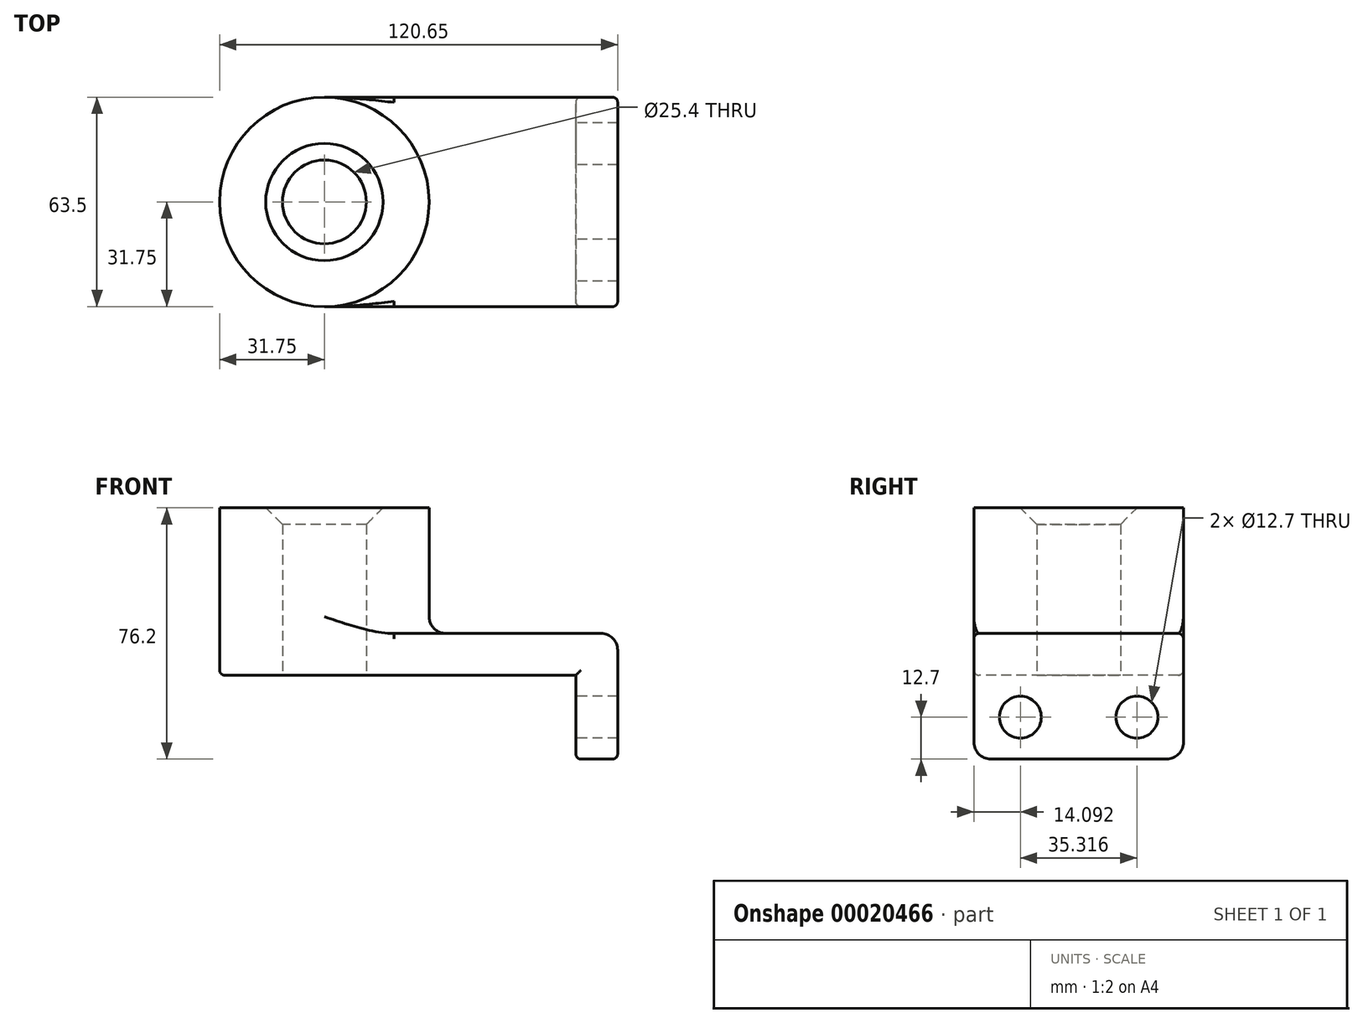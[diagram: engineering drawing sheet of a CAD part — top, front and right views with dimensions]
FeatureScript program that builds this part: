
annotation { "Feature Type Name" : "Feature", "Feature Type Description" : "" }
export const myFeature = defineFeature(function(context is Context, id is Id, definition is map)
    precondition{}
    {
        {
            var Q0;
            Q0=qCreatedBy(makeId("Top.planeOp"),FACE);
            var sketch = newSketch(context, id + "F0", { "sketchPlane" : qUnion([Q0])});
            skLineSegment(sketch, "E0.rect.bottom", {"start": v(-38.1, 31.75) * mm, "end": v(38.1, 31.75) * mm});
            skLineSegment(sketch, "E0.rect.top", {"start": v(-38.1, -31.75) * mm, "end": v(38.1, -31.75) * mm});
            skLineSegment(sketch, "E0.rect.left", {"start": v(-38.1, 31.75) * mm, "end": v(-38.1, -31.75) * mm});
            skLineSegment(sketch, "E0.rect.right", {"start": v(38.1, 31.75) * mm, "end": v(38.1, -31.75) * mm});
            skPoint(sketch, "E0.rect.middle", {"position": v(0, 0) * mm});
            skCircle(sketch, "E1", {"center": v(-38.1, 0) * mm, "radius": 31.75 * mm});
            skCircle(sketch, "E2", {"center": v(-38.1, 0) * mm, "radius": 12.7 * mm});
            skSolve(sketch);
        }
        {
            var Q0;
            {var subQ3=sQuery(id+"F0.wireOp",EDGE,"E0.rect.bottom");Q0=makeQuery(id+"F0.imprint","IMPRINT",FACE,{"disambiguationData":[TD([[makeQuery(id+"F0.imprint","IMPRINT",EDGE,{"derivedFrom":subQ3}),-1.0]])]});}
            var Q1;
            {var subQ0=sQuery(id+"F0.wireOp",EDGE,"E2");var subQ1=sQuery(id+"F0.wireOp",EDGE,"E0.rect.left");var subQ3=makeQuery(id+"F0.imprint","INTERSECT",VERTEX,{"disambiguationData":[OD(0.0)],"derivedFrom":[subQ1,subQ0]});Q1=makeQuery(id+"F0.imprint","IMPRINT",FACE,{"disambiguationData":[TD([[makeQuery(id+"F0.imprint","IMPRINT",EDGE,{"disambiguationData":[TD([[subQ3,-1.0]])],"derivedFrom":subQ0}),-1.0]])]});}
            var Q2;
            {var subQ0=sQuery(id+"F0.wireOp",EDGE,"E2");var subQ1=sQuery(id+"F0.wireOp",EDGE,"E0.rect.left");var subQ3=makeQuery(id+"F0.imprint","INTERSECT",VERTEX,{"disambiguationData":[OD(0.0)],"derivedFrom":[subQ1,subQ0]});Q2=makeQuery(id+"F0.imprint","IMPRINT",FACE,{"disambiguationData":[TD([[makeQuery(id+"F0.imprint","IMPRINT",EDGE,{"disambiguationData":[TD([[subQ3,1.0]])],"derivedFrom":subQ0}),-1.0]])]});}
            extrude(context, id + "F1", {"entities" : qUnion([Q0, Q1, Q2]), "depth" : 12.7 * mm});
        }
        {
            var Q0;
            {var subQ0=sQuery(id+"F0.wireOp",EDGE,"E2");var subQ1=sQuery(id+"F0.wireOp",EDGE,"E0.rect.left");var subQ3=makeQuery(id+"F0.imprint","INTERSECT",VERTEX,{"disambiguationData":[OD(0.0)],"derivedFrom":[subQ1,subQ0]});Q0=makeQuery(id+"F0.imprint","IMPRINT",FACE,{"disambiguationData":[TD([[makeQuery(id+"F0.imprint","IMPRINT",EDGE,{"disambiguationData":[TD([[subQ3,-1.0]])],"derivedFrom":subQ0}),-1.0]])]});}
            var Q1;
            {var subQ0=sQuery(id+"F0.wireOp",EDGE,"E2");var subQ1=sQuery(id+"F0.wireOp",EDGE,"E0.rect.left");var subQ3=makeQuery(id+"F0.imprint","INTERSECT",VERTEX,{"disambiguationData":[OD(0.0)],"derivedFrom":[subQ1,subQ0]});Q1=makeQuery(id+"F0.imprint","IMPRINT",FACE,{"disambiguationData":[TD([[makeQuery(id+"F0.imprint","IMPRINT",EDGE,{"disambiguationData":[TD([[subQ3,1.0]])],"derivedFrom":subQ0}),-1.0]])]});}
            extrude(context, id + "F2", {"entities" : qUnion([Q0, Q1]), "operationType" : NewBodyOperationType.ADD, "depth" : 50.8 * mm});
        }
        {
            var Q0;
            Q0=makeQuery(id+"F1.opExtrude","SWEPT_FACE",FACE,{"disambiguationData":[OSD([sQuery(id+"F0.wireOp",EDGE,"E0.rect.right")])]});
            var sketch = newSketch(context, id + "F3", { "sketchPlane" : qUnion([Q0])});
            skLineSegment(sketch, "E3.bottom", {"start": v(-31.75, 12.7) * mm, "end": v(31.75, 12.7) * mm});
            skLineSegment(sketch, "E3.top", {"start": v(-31.75, -25.4) * mm, "end": v(31.75, -25.4) * mm});
            skLineSegment(sketch, "E3.left", {"start": v(-31.75, 12.7) * mm, "end": v(-31.75, -25.4) * mm});
            skLineSegment(sketch, "E3.right", {"start": v(31.75, 12.7) * mm, "end": v(31.75, -25.4) * mm});
            skCircle(sketch, "E4", {"center": v(-17.66, -12.7) * mm, "radius": 6.35 * mm});
            skLineSegment(sketch, "E5", {"start": v(0, 0) * mm, "end": v(0, -25.4) * mm, "construction": true});
            skCircle(sketch, "E6.MirrorC", {"center": v(17.66, -12.7) * mm, "radius": 6.35 * mm});
            skSolve(sketch);
        }
        {
            var Q0;
            {var subQ2=sQuery(id+"F3.wireOp",EDGE,"E3.top");Q0=makeQuery(id+"F3.imprint","IMPRINT",FACE,{"disambiguationData":[TD([[makeQuery(id+"F3.imprint","IMPRINT",EDGE,{"derivedFrom":subQ2}),1.0]])]});}
            var Q1;
            {var subQ2=sQuery(id+"F3.wireOp",EDGE,"E3.bottom");Q1=makeQuery(id+"F3.imprint","IMPRINT",FACE,{"disambiguationData":[TD([[makeQuery(id+"F3.imprint","IMPRINT",EDGE,{"derivedFrom":subQ2}),1.0]])]});}
            extrude(context, id + "F4", {"entities" : qUnion([Q0, Q1]), "operationType" : NewBodyOperationType.ADD, "depth" : 12.7 * mm});
        }
        {
            var Q0;
            {var subQ0=sQuery(id+"F0.wireOp",EDGE,"E1");Q0=makeQuery(id+"F2.boolean.opBoolean","INTERSECT",EDGE,{"derivedFrom":[makeQuery(id+"F1.opExtrude","CAP_FACE",FACE,{"disambiguationData":[OSD([sQuery(id+"F0.wireOp",EDGE,"E0.rect.bottom"),sQuery(id+"F0.wireOp",EDGE,"E0.rect.top"),sQuery(id+"F0.wireOp",EDGE,"E0.rect.right"),subQ0,sQuery(id+"F0.wireOp",EDGE,"E2")])],"isStart":false}),makeQuery(id+"F2.opExtrude","SWEPT_FACE",FACE,{"disambiguationData":[OSD([subQ0])]})]});}
            var Q1;
            Q1=makeQuery(id+"F4.opExtrude","CAP_EDGE",EDGE,{"disambiguationData":[OSD([sQuery(id+"F3.wireOp",EDGE,"E3.bottom")])],"isStart":false});
            var Q2;
            Q2=makeQuery(id+"F4.opExtrude","SWEPT_EDGE",EDGE,{"disambiguationData":[OSD([sQuery(id+"F3.wireOp",EDGE,"E3.top"),sQuery(id+"F3.wireOp",EDGE,"E3.right")])]});
            var Q3;
            Q3=makeQuery(id+"F4.opExtrude","SWEPT_EDGE",EDGE,{"disambiguationData":[OSD([sQuery(id+"F3.wireOp",EDGE,"E3.top"),sQuery(id+"F3.wireOp",EDGE,"E3.left")])]});
            fillet(context, id + "F5", {"entities" : qUnion([Q0, Q1, Q2, Q3]), "radius" : 5.08 * mm, "tangentPropagation" : true, "allowEdgeOverflow" : false});
        }
        {
            var Q0;
            Q0=makeQuery(id+"F4.boolean.opBoolean","MERGE",EDGE,{"derivedFrom":[makeQuery(id+"F1.opExtrude","CAP_EDGE",EDGE,{"disambiguationData":[OSD([sQuery(id+"F0.wireOp",EDGE,"E0.rect.top")])],"isStart":false}),makeQuery(id+"F4.opExtrude","SWEPT_EDGE",EDGE,{"disambiguationData":[OSD([sQuery(id+"F3.wireOp",EDGE,"E3.bottom"),sQuery(id+"F3.wireOp",EDGE,"E3.left")])]})]});
            var Q1;
            Q1=makeQuery(id+"F1.opExtrude","CAP_EDGE",EDGE,{"disambiguationData":[OSD([sQuery(id+"F0.wireOp",EDGE,"E0.rect.top")])],"isStart":true});
            var Q2;
            Q2=makeQuery(id+"F4.opExtrude","CAP_EDGE",EDGE,{"disambiguationData":[OSD([sQuery(id+"F3.wireOp",EDGE,"E3.right")])],"isStart":true});
            var Q3;
            {var subQ0=sQuery(id+"F3.wireOp",EDGE,"E3.top");var subQ1=sQuery(id+"F3.wireOp",EDGE,"E3.right");Q3=makeQuery(id+"F5.opFillet","BLEND_EDGE",EDGE,{"blendedFrom":[makeQuery(id+"F4.opExtrude","SWEPT_EDGE",EDGE,{"disambiguationData":[OSD([subQ0,subQ1])]}),makeQuery(id+"F4.opExtrude","CAP_FACE",FACE,{"disambiguationData":[OSD([sQuery(id+"F3.wireOp",EDGE,"E3.bottom"),subQ0,sQuery(id+"F3.wireOp",EDGE,"E3.left"),subQ1,sQuery(id+"F3.wireOp",EDGE,"E4"),sQuery(id+"F3.wireOp",EDGE,"E6.MirrorC")])],"isStart":true})],"blendedInto":[makeQuery(id+"F4.opExtrude","CAP_FACE",FACE,{"disambiguationData":[OSD([sQuery(id+"F3.wireOp",EDGE,"E3.bottom"),subQ0,sQuery(id+"F3.wireOp",EDGE,"E3.left"),subQ1,sQuery(id+"F3.wireOp",EDGE,"E4"),sQuery(id+"F3.wireOp",EDGE,"E6.MirrorC")])],"isStart":true})]});}
            var Q4;
            Q4=makeQuery(id+"F4.opExtrude","CAP_EDGE",EDGE,{"disambiguationData":[OSD([sQuery(id+"F3.wireOp",EDGE,"E3.top")])],"isStart":true});
            fillet(context, id + "F6", {"entities" : qUnion([Q0, Q1, Q2, Q3, Q4]), "radius" : 1.59 * mm, "tangentPropagation" : true, "allowEdgeOverflow" : false});
        }
        {
            var Q0;
            Q0=makeQuery(id+"F2.opExtrude","CAP_EDGE",EDGE,{"disambiguationData":[OSD([sQuery(id+"F0.wireOp",EDGE,"E2")])],"isStart":false});
            chamfer(context, id + "F7", {"entities" : qUnion([Q0]), "width" : 5.08 * mm, "tangentPropagation" : true});
        }
    });
